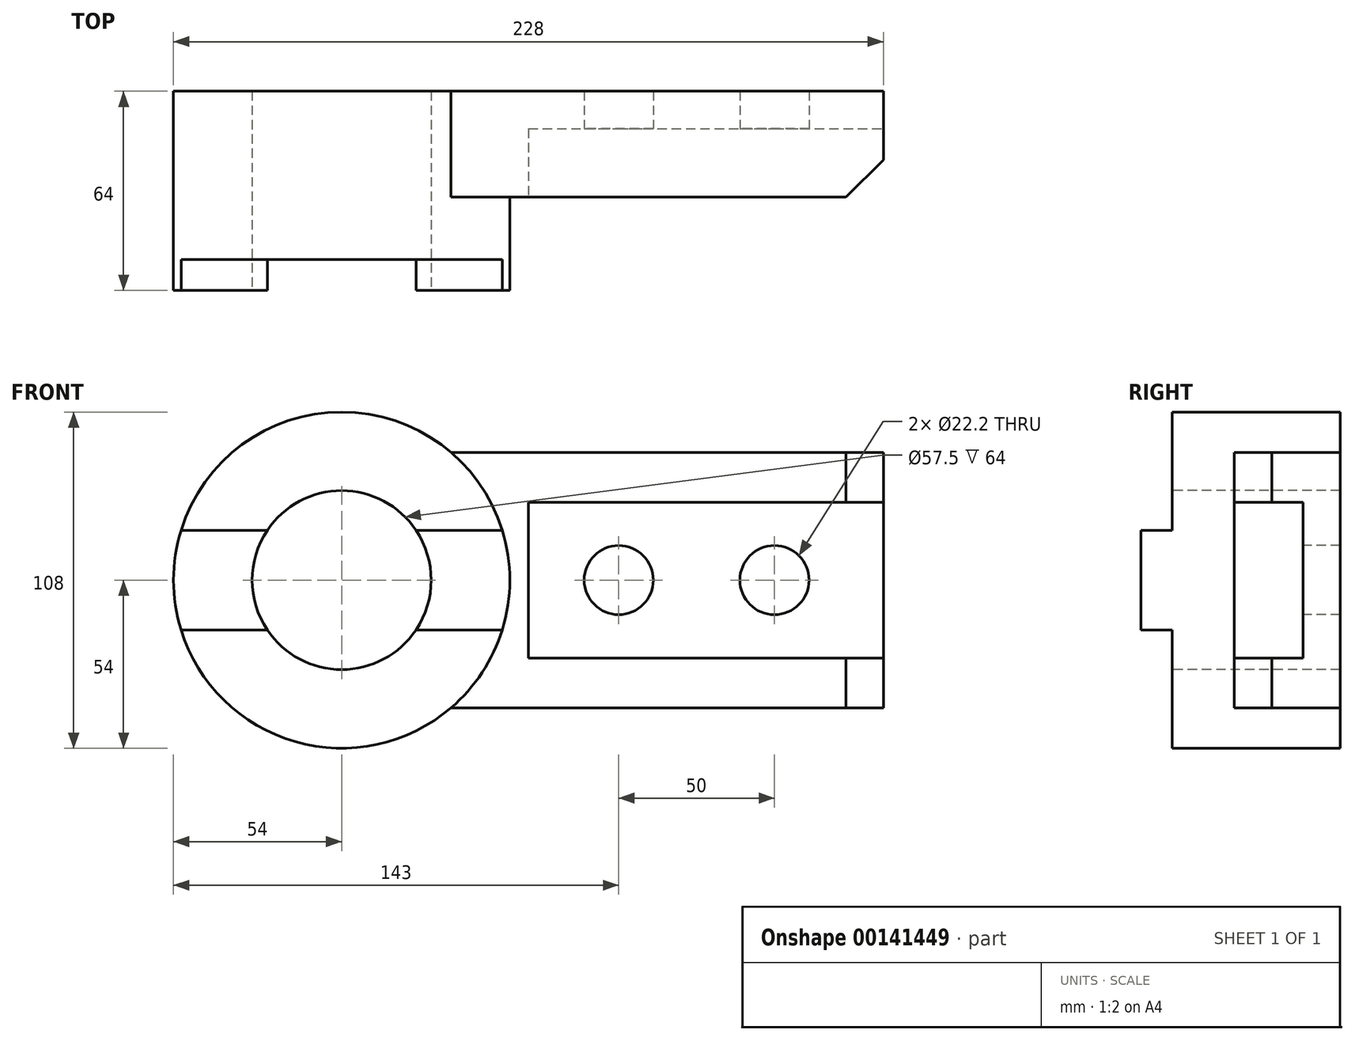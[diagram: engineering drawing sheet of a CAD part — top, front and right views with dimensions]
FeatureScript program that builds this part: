
annotation { "Feature Type Name" : "Feature", "Feature Type Description" : "" }
export const myFeature = defineFeature(function(context is Context, id is Id, definition is map)
    precondition{}
    {
        {
            var Q0;
            Q0=qCreatedBy(makeId("Front.planeOp"),FACE);
            var sketch = newSketch(context, id + "F0", { "sketchPlane" : qUnion([Q0])});
            skCircle(sketch, "E0", {"center": v(0, 0) * mm, "radius": 28.75 * mm});
            skCircle(sketch, "E1", {"center": v(0, 0) * mm, "radius": 54 * mm});
            skSolve(sketch);
        }
        {
            var Q0;
            Q0 = qSketchRegion(id + "F0", true);
            extrude(context, id + "F1", {"entities" : qUnion([Q0]), "oppositeDirection" : true, "depth" : 64 * mm});
        }
        {
            var Q0;
            Q0=makeQuery(id+"F1.opExtrude","CAP_FACE",FACE,{"disambiguationData":[OSD([sQuery(id+"F0.wireOp",EDGE,"E0"),sQuery(id+"F0.wireOp",EDGE,"E1")])],"isStart":true});
            var sketch = newSketch(context, id + "F2", { "sketchPlane" : qUnion([Q0])});
            skArc(sketch, "E2.0", {"start": v(-23.89, -16) * mm, "mid": v(0, -28.75) * mm, "end": v(23.89, -16) * mm});
            skArc(sketch, "E3.0", {"start": v(-51.58, -16) * mm, "mid": v(0, -54) * mm, "end": v(51.58, -16) * mm});
            skLineSegment(sketch, "E4", {"start": v(-51.58, 16) * mm, "end": v(-23.89, 16) * mm});
            skLineSegment(sketch, "E5", {"start": v(-51.58, -16) * mm, "end": v(-23.89, -16) * mm});
            skLineSegment(sketch, "E6", {"start": v(23.89, 16) * mm, "end": v(51.58, 16) * mm});
            skLineSegment(sketch, "E7", {"start": v(23.89, -16) * mm, "end": v(51.58, -16) * mm});
            skPoint(sketch, "E8", {"position": v(-54, 0) * mm});
            skArc(sketch, "E9.trimOffspring", {"start": v(23.89, 16) * mm, "mid": v(0, 28.75) * mm, "end": v(-23.89, 16) * mm});
            skArc(sketch, "E10.trimOffspring", {"start": v(51.58, 16) * mm, "mid": v(0, 54) * mm, "end": v(-51.58, 16) * mm});
            skSolve(sketch);
        }
        {
            var Q0;
            Q0 = qSketchRegion(id + "F2", true);
            extrude(context, id + "F3", {"entities" : qUnion([Q0]), "operationType" : NewBodyOperationType.REMOVE, "oppositeDirection" : true, "depth" : 10 * mm});
        }
        {
            var Q0;
            Q0=makeQuery(id+"F3.boolean.opBoolean","COPY",FACE,{"derivedFrom":makeQuery(id+"F3.opExtrude","CAP_FACE",FACE,{"disambiguationData":[OSD([sQuery(id+"F2.wireOp",EDGE,"E2.0"),sQuery(id+"F2.wireOp",EDGE,"E3.0"),sQuery(id+"F2.wireOp",EDGE,"E5"),sQuery(id+"F2.wireOp",EDGE,"E7")])],"isStart":false})});
            var sketch = newSketch(context, id + "F4", { "sketchPlane" : qUnion([Q0])});
            skLineSegment(sketch, "E11", {"start": v(35.14, -41) * mm, "end": v(174, -41) * mm});
            skLineSegment(sketch, "E12", {"start": v(174, -41) * mm, "end": v(174, 41) * mm});
            skLineSegment(sketch, "E13", {"start": v(174, 41) * mm, "end": v(35.14, 41) * mm});
            skCircle(sketch, "E14", {"center": v(89, 0) * mm, "radius": 11.1 * mm});
            skCircle(sketch, "E15", {"center": v(139, 0) * mm, "radius": 11.1 * mm});
            skPoint(sketch, "E16", {"position": v(0, 54) * mm});
            skArc(sketch, "E17.0", {"start": v(51.58, 16) * mm, "mid": v(45.12, 29.66) * mm, "end": v(35.14, 41) * mm});
            skArc(sketch, "E18.0", {"start": v(51.58, -16) * mm, "mid": v(54, 0) * mm, "end": v(51.58, 16) * mm});
            skArc(sketch, "E19.0", {"start": v(35.14, -41) * mm, "mid": v(45.12, -29.66) * mm, "end": v(51.58, -16) * mm});
            skPoint(sketch, "E20.orphan", {"position": v(-51.58, 16) * mm});
            skPoint(sketch, "E21.orphan", {"position": v(-51.58, -16) * mm});
            skLineSegment(sketch, "E22", {"start": v(0, 0) * mm, "end": v(174, 0) * mm, "construction": true});
            skSolve(sketch);
        }
        {
            var Q0;
            Q0 = qSketchRegion(id + "F4", true);
            var Q1;
            Q1=makeQuery(id+"F1.opExtrude","CAP_FACE",FACE,{"disambiguationData":[OSD([sQuery(id+"F0.wireOp",EDGE,"E0"),sQuery(id+"F0.wireOp",EDGE,"E1")])],"isStart":false});
            extrude(context, id + "F5", {"entities" : qUnion([Q0]), "operationType" : NewBodyOperationType.ADD, "endBound" : BoundingType.UP_TO_SURFACE, "oppositeDirection" : true, "endBoundEntityFace" : qUnion([Q1]), "depth" : 25 * mm});
        }
        {
            var Q0;
            Q0 = qSketchRegion(id + "F4", true);
            extrude(context, id + "F6", {"entities" : qUnion([Q0]), "operationType" : NewBodyOperationType.REMOVE, "oppositeDirection" : true, "depth" : 20 * mm});
        }
        {
            var Q0;
            Q0=makeQuery(id+"F5.opExtrude","SWEPT_FACE",FACE,{"disambiguationData":[OSD([sQuery(id+"F4.wireOp",EDGE,"E13")])]});
            var sketch = newSketch(context, id + "F7", { "sketchPlane" : qUnion([Q0])});
            skLineSegment(sketch, "E23", {"start": v(162, 30) * mm, "end": v(174, 42) * mm});
            skLineSegment(sketch, "E24", {"start": v(174, 42) * mm, "end": v(174, 30) * mm});
            skLineSegment(sketch, "E25", {"start": v(174, 30) * mm, "end": v(162, 30) * mm});
            skSolve(sketch);
        }
        {
            var Q0;
            Q0 = qSketchRegion(id + "F7", true);
            extrude(context, id + "F8", {"entities" : qUnion([Q0]), "operationType" : NewBodyOperationType.REMOVE, "endBound" : BoundingType.THROUGH_ALL, "oppositeDirection" : true, "depth" : 25 * mm});
        }
        {
            var Q0;
            Q0=makeQuery(id+"F6.boolean.opBoolean","COPY",FACE,{"derivedFrom":makeQuery(id+"F6.opExtrude","CAP_FACE",FACE,{"disambiguationData":[OSD([sQuery(id+"F4.wireOp",EDGE,"E11"),sQuery(id+"F4.wireOp",EDGE,"E12"),sQuery(id+"F4.wireOp",EDGE,"E13"),sQuery(id+"F4.wireOp",EDGE,"E14"),sQuery(id+"F4.wireOp",EDGE,"E15"),sQuery(id+"F4.wireOp",EDGE,"E17.0"),sQuery(id+"F4.wireOp",EDGE,"E18.0"),sQuery(id+"F4.wireOp",EDGE,"E19.0")])],"isStart":false})});
            var sketch = newSketch(context, id + "F9", { "sketchPlane" : qUnion([Q0])});
            skLineSegment(sketch, "E26.bottom", {"start": v(60, -25) * mm, "end": v(174, -25) * mm});
            skLineSegment(sketch, "E26.top", {"start": v(60, 25) * mm, "end": v(174, 25) * mm});
            skLineSegment(sketch, "E26.left", {"start": v(60, -25) * mm, "end": v(60, 25) * mm});
            skLineSegment(sketch, "E26.right", {"start": v(174, -25) * mm, "end": v(174, 25) * mm});
            skSolve(sketch);
        }
        {
            var Q0;
            Q0 = qSketchRegion(id + "F9", true);
            extrude(context, id + "F10", {"entities" : qUnion([Q0]), "operationType" : NewBodyOperationType.REMOVE, "oppositeDirection" : true, "depth" : 22 * mm});
        }
    });
